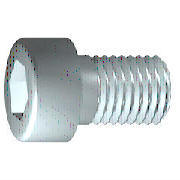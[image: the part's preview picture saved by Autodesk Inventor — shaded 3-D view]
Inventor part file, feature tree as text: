
AUTODESK INVENTOR PART (.ipt)
format: ipt  version: 2013 (Build 170138000, 138)  size: 183,808 bytes
history: native  units: mm (DEFAULTED — no unit token found)
features: sketch x2, extrude x1, plane x1, fillet x1
ambient origin geometry x7: Origin, YZ Plane, XY Plane, X Axis, Y Axis, Z Axis, Center Point
bodies: Solid1 (feature_tree), Body (feature_tree)
feature tree (5):
  extrude  "Slot"  Depth=0.306825mm
  plane  "Work Plane1"
  fillet  "Fillet2"  Radius=3.0mm
  sketch  "Sketch1"  dims[d1=19.08655mm d2=0.306825mm d3=3.0mm]
  sketch  "Sketch2"  dims[d4=1.5mm d5=60.0deg d6=3.0mm d7=3.0mm d8=2.886751mm d9=5.5mm d10=90.0deg d11=10.0mm d12=0.0mm d13=19.08655mm d14=0.0mm d15=0.306725mm d16=0.306725mm d17=0.3mm d19=0.0mm d26=20.0mm d27=45.0deg d28=0.0mm d29=0.0mm d30=0.1mm]
